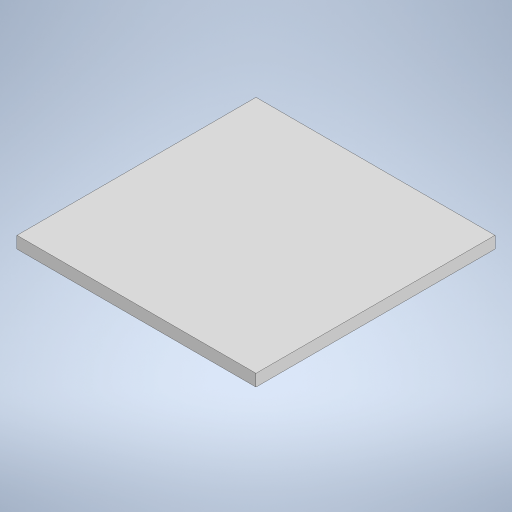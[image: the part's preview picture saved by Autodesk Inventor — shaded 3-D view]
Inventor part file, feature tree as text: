
AUTODESK INVENTOR PART (.ipt)
format: ipt  version: 2024 (Build 280153000, 153)  size: 241,152 bytes
history: native  units: in
note: dims shown in document units (in); Inventor stores cm internally (conversion verified against a paired STEP export)
features: extrude x3, sketch x3
ambient origin geometry x8: Origin, YZ Plane, XZ Plane, XY Plane, X Axis, Y Axis, Z Axis, Center Point
bodies: Body1 (feature_tree)
feature tree (6):
  extrude  "Extrusion35"  Depth=0.1181in TaperAngle=0.0deg
  extrude  "Extrusion36"  Depth=1.5748in
  extrude  "Extrusion37"  Depth=0.0394in
  sketch  "Sketch46"  dims[d158=0.1181in d159=0.1181in d160=0.0in]
  sketch  "Sketch47"  dims[d161=1.5748in d162=1.5748in]
  sketch  "Sketch48"  dims[d163=0.0787in d164=0.0in d165=0.1476in d166=0.0394in d167=0.0in d42=0.0197in d43=0.0344in d44=0.0197in d45=0.0344in d46=0.0in d47=0.0in d48=0.0in d49=0.0in d50=0.0in d51=0.0in d52=0.0in d53=0.0in d55=0.0197in d56=0.0344in d57=0.0197in d58=0.0344in d60=0.0197in d61=0.0344in d62=0.0197in d63=0.0344in d72=0.0197in d73=0.0344in d74=0.0197in d75=0.0344in d124=0.0197in d125=0.0344in d126=0.0197in d127=0.0344in d128=0.0344in d129=0.0197in d130=0.0344in d136=0.0197in d137=0.0344in d138=0.0197in d139=0.0344in]
